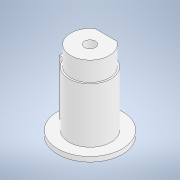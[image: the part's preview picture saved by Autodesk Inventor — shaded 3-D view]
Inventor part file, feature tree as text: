
AUTODESK INVENTOR PART (.ipt)
format: ipt  version: 2020.4 (Build 244396000, 396)  size: 150,016 bytes
history: native  units: mm
features: sketch x5, extrude x4, hole x1
ambient origin geometry x8: Origin, YZ Plane, XZ Plane, XY Plane, X Axis, Y Axis, Z Axis, Center Point
bodies: Solid1 (feature_tree)
feature tree (10):
  extrude  "Extrusion1"  Depth=17.0mm TaperAngle=0.0deg
  extrude  "Extrusion2"  Depth=20.0mm TaperAngle=0.0deg
  extrude  "Extrusion3"  Depth=3.5mm
  hole  "Hole1"  [1 undecoded]
  extrude  "Extrusion4"  Depth=10.0mm
  sketch  "Sketch1"  dims[d0=13.0mm d1=17.0mm d2=0.0mm]
  sketch  "Sketch2"  dims[d3=20.0mm d4=1.5mm d5=0.0mm]
  sketch  "Sketch4"  dims[d8=1.5mm d9=3.5mm]
  sketch  "Sketch5"  dims[d10=12.0mm d11=6.0mm d12=0.0mm]
  sketch  "Sketch6"  dims[d13=3.4mm d14=6.0mm d15=11.0mm d16=2.6mm d17=90.0deg d18=9.0mm d19=20.594885mm d21=1.5mm d24=10.0mm d25=0.0mm d26=3.0mm d27=5.0mm]
note: 1 required parameter value undecoded (feature->parameter linkage not recoverable at this tier; creation-order binding heuristic only, values carry confidence <= 0.55)
